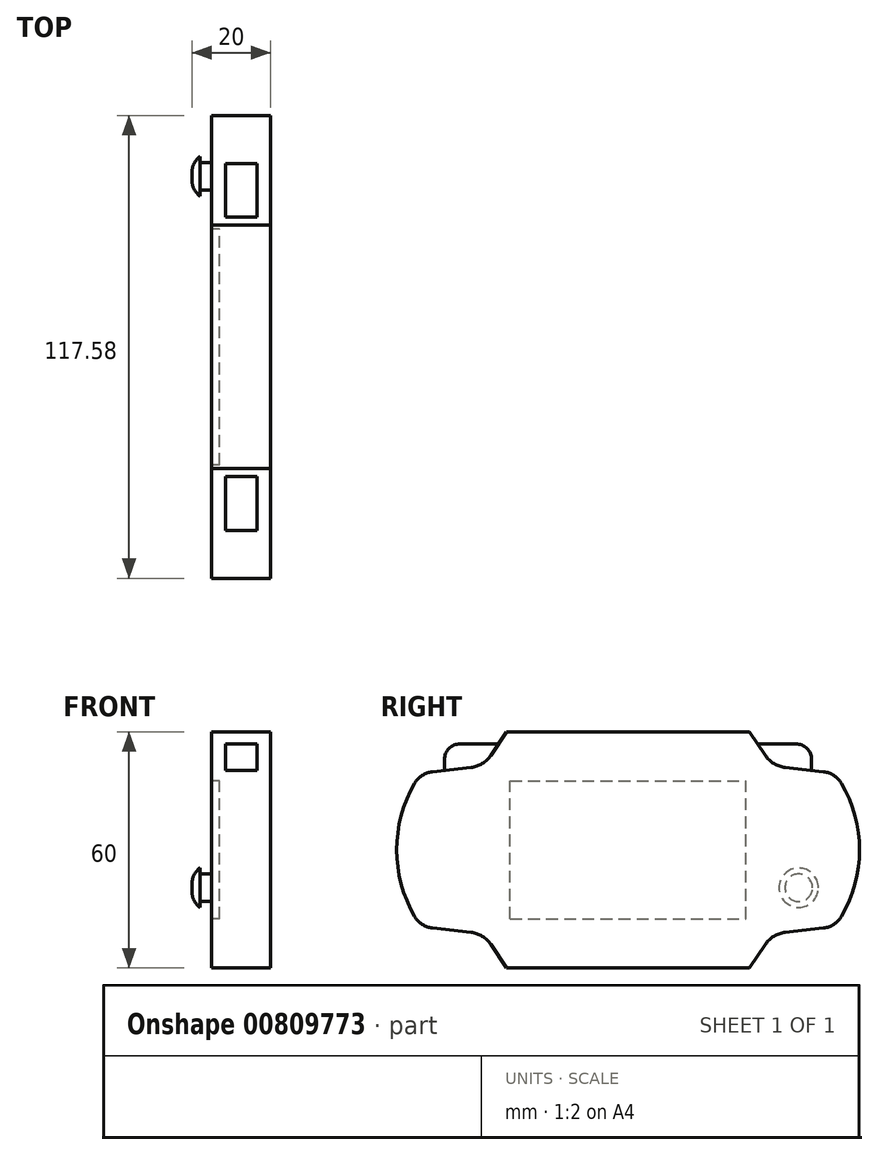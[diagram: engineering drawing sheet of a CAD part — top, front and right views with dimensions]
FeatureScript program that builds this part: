
annotation { "Feature Type Name" : "Feature", "Feature Type Description" : "" }
export const myFeature = defineFeature(function(context is Context, id is Id, definition is map)
    precondition{}
    {
        {
            var Q0;
            Q0=qCreatedBy(makeId("Right.planeOp"),FACE);
            var sketch = newSketch(context, id + "F0", { "sketchPlane" : qUnion([Q0])});
            skLineSegment(sketch, "E0.bottom", {"start": v(-30.9, -30) * mm, "end": v(30.9, -30) * mm});
            skLineSegment(sketch, "E0.top", {"start": v(-30.9, 30) * mm, "end": v(30.9, 30) * mm});
            skLineSegment(sketch, "E0.left", {"start": v(-52.5, -19.53) * mm, "end": v(-52.5, 19.53) * mm});
            skLineSegment(sketch, "E0.right", {"start": v(52.5, -19.53) * mm, "end": v(52.5, 19.53) * mm});
            skPoint(sketch, "E0.middle", {"position": v(0, 0) * mm});
            skLineSegment(sketch, "E1", {"start": v(49.7, 19.85) * mm, "end": v(46.21, 20.24) * mm});
            skLineSegment(sketch, "E2", {"start": v(34.87, 24.03) * mm, "end": v(30.9, 30) * mm});
            skPoint(sketch, "E3.visualSharp", {"position": v(36.68, 21.3) * mm});
            skArc(sketch, "E3.filletArc", {"start": v(34.87, 24.03) * mm, "mid": v(37.06, 21.92) * mm, "end": v(39.92, 20.94) * mm});
            skLineSegment(sketch, "E4", {"start": v(0, 39.51) * mm, "end": v(0, -39.4) * mm});
            skLineSegment(sketch, "E5.MirrorCS", {"start": v(-34.87, 24.03) * mm, "end": v(-30.9, 30) * mm});
            skPoint(sketch, "E6.MirrorP", {"position": v(-36.68, 21.3) * mm});
            skLineSegment(sketch, "E7.MirrorCS", {"start": v(-49.7, 19.85) * mm, "end": v(-46.21, 20.24) * mm});
            skArc(sketch, "E8.MirrorCS", {"start": v(-34.87, 24.03) * mm, "mid": v(-37.06, 21.92) * mm, "end": v(-39.92, 20.94) * mm});
            skLineSegment(sketch, "E9", {"start": v(46.21, 20.24) * mm, "end": v(39.92, 20.94) * mm});
            skLineSegment(sketch, "E10", {"start": v(59.6, 0) * mm, "end": v(-64.27, 0) * mm});
            skLineSegment(sketch, "E11.MirrorCS", {"start": v(49.7, -19.85) * mm, "end": v(46.21, -20.24) * mm});
            skLineSegment(sketch, "E12.MirrorCS", {"start": v(46.21, -20.24) * mm, "end": v(39.92, -20.94) * mm});
            skPoint(sketch, "E13.MirrorP", {"position": v(36.68, -21.3) * mm});
            skLineSegment(sketch, "E14.MirrorCS", {"start": v(34.87, -24.03) * mm, "end": v(30.9, -30) * mm});
            skArc(sketch, "E15.MirrorCS", {"start": v(34.87, -24.03) * mm, "mid": v(37.06, -21.92) * mm, "end": v(39.92, -20.94) * mm});
            skLineSegment(sketch, "E16.MirrorCS", {"start": v(-34.87, -24.03) * mm, "end": v(-30.9, -30) * mm});
            skArc(sketch, "E17.MirrorCS", {"start": v(-34.87, -24.03) * mm, "mid": v(-37.06, -21.92) * mm, "end": v(-39.92, -20.94) * mm});
            skLineSegment(sketch, "E18.MirrorCS", {"start": v(-49.7, -19.85) * mm, "end": v(-46.21, -20.24) * mm});
            skLineSegment(sketch, "E19", {"start": v(-46.21, 20.24) * mm, "end": v(-39.92, 20.94) * mm});
            skLineSegment(sketch, "E20", {"start": v(-46.21, -20.24) * mm, "end": v(-39.92, -20.94) * mm});
            skArc(sketch, "E21", {"start": v(54.2, -16.92) * mm, "mid": v(58.79, 0) * mm, "end": v(54.2, 16.92) * mm});
            skArc(sketch, "E22.MirrorCS", {"start": v(-54.2, -16.92) * mm, "mid": v(-58.79, 0) * mm, "end": v(-54.2, 16.92) * mm});
            skPoint(sketch, "E23.visualSharp", {"position": v(52.5, 19.53) * mm});
            skArc(sketch, "E23.filletArc", {"start": v(54.2, 16.92) * mm, "mid": v(52.3, 18.92) * mm, "end": v(49.7, 19.85) * mm});
            skPoint(sketch, "E24.visualSharp", {"position": v(52.5, -19.53) * mm});
            skArc(sketch, "E24.filletArc", {"start": v(49.7, -19.85) * mm, "mid": v(52.3, -18.92) * mm, "end": v(54.2, -16.92) * mm});
            skPoint(sketch, "E25.visualSharp", {"position": v(-52.5, 19.53) * mm});
            skArc(sketch, "E25.filletArc", {"start": v(-49.7, 19.85) * mm, "mid": v(-52.3, 18.92) * mm, "end": v(-54.2, 16.92) * mm});
            skPoint(sketch, "E26.visualSharp", {"position": v(-52.5, -19.53) * mm});
            skArc(sketch, "E26.filletArc", {"start": v(-54.2, -16.92) * mm, "mid": v(-52.3, -18.92) * mm, "end": v(-49.7, -19.85) * mm});
            skPoint(sketch, "E27.orphan", {"position": v(52.5, 30) * mm});
            skPoint(sketch, "E28.orphan", {"position": v(52.5, -30) * mm});
            skPoint(sketch, "E29.orphan", {"position": v(-52.5, -30) * mm});
            skPoint(sketch, "E30.orphan", {"position": v(-52.5, 30) * mm});
            skSolve(sketch);
        }
        {
            var Q0;
            Q0 = qSketchRegion(id + "F0", true);
            extrude(context, id + "F1", {"entities" : qUnion([Q0]), "endBound" : BoundingType.SYMMETRIC, "depth" : 15 * mm, "offsetDistance" : 25 * mm});
        }
        {
            var Q0;
            Q0=qCreatedBy(makeId("Right.planeOp"),FACE);
            var sketch = newSketch(context, id + "F2", { "sketchPlane" : qUnion([Q0])});
            skLineSegment(sketch, "E31.bottom", {"start": v(29.71, 18.85) * mm, "end": v(46.63, 18.85) * mm});
            skLineSegment(sketch, "E31.top", {"start": v(29.71, 26.92) * mm, "end": v(42.63, 26.92) * mm});
            skLineSegment(sketch, "E31.left", {"start": v(29.71, 18.85) * mm, "end": v(29.71, 26.92) * mm});
            skLineSegment(sketch, "E31.right", {"start": v(46.63, 18.85) * mm, "end": v(46.63, 22.92) * mm});
            skPoint(sketch, "E31.middle", {"position": v(38.17, 22.88) * mm});
            skLineSegment(sketch, "E32", {"start": v(0, 47.3) * mm, "end": v(0, -44.62) * mm});
            skLineSegment(sketch, "E33.MirrorCS", {"start": v(-29.71, 26.92) * mm, "end": v(-42.63, 26.92) * mm});
            skLineSegment(sketch, "E34.MirrorCS", {"start": v(-46.63, 18.85) * mm, "end": v(-46.63, 22.92) * mm});
            skLineSegment(sketch, "E35.MirrorCS", {"start": v(-29.71, 18.85) * mm, "end": v(-29.71, 26.92) * mm});
            skLineSegment(sketch, "E36.MirrorCS", {"start": v(-29.71, 18.85) * mm, "end": v(-46.63, 18.85) * mm});
            skPoint(sketch, "E37.visualSharp", {"position": v(46.63, 26.92) * mm});
            skArc(sketch, "E37.filletArc", {"start": v(46.63, 22.92) * mm, "mid": v(45.46, 25.75) * mm, "end": v(42.63, 26.92) * mm});
            skPoint(sketch, "E38.visualSharp", {"position": v(-46.63, 26.92) * mm});
            skArc(sketch, "E38.filletArc", {"start": v(-42.63, 26.92) * mm, "mid": v(-45.46, 25.75) * mm, "end": v(-46.63, 22.92) * mm});
            skSolve(sketch);
        }
        {
            var Q0;
            Q0=makeQuery(id+"F2.imprint","IMPRINT",FACE,{"disambiguationData":[TD([[makeQuery(id+"F2.imprint","IMPRINT",EDGE,{"derivedFrom":sQuery(id+"F2.wireOp",EDGE,"E31.bottom")}),1.0]])]});
            var Q1;
            Q1=makeQuery(id+"F2.imprint","IMPRINT",FACE,{"disambiguationData":[TD([[makeQuery(id+"F2.imprint","IMPRINT",EDGE,{"derivedFrom":sQuery(id+"F2.wireOp",EDGE,"E33.MirrorCS")}),1.0]])]});
            var Q2;
            Q2 = qConstructionFilter(qBodyType(qCreatedBy(id + "F2" ,EDGE), BodyType.WIRE), ConstructionObject.NO);
            extrude(context, id + "F3", {"entities" : qUnion([Q0, Q1]), "operationType" : NewBodyOperationType.ADD, "surfaceEntities" : qUnion([Q2]), "endBound" : BoundingType.SYMMETRIC, "depth" : 8 * mm, "offsetDistance" : 25 * mm});
        }
        {
            var Q0;
            Q0=makeQuery(id+"F1.opExtrude","CAP_FACE",FACE,{"disambiguationData":[OSD([sQuery(id+"F0.wireOp",EDGE,"E0.bottom"),sQuery(id+"F0.wireOp",EDGE,"E0.top"),sQuery(id+"F0.wireOp",EDGE,"E1"),sQuery(id+"F0.wireOp",EDGE,"E2"),sQuery(id+"F0.wireOp",EDGE,"E3.filletArc"),sQuery(id+"F0.wireOp",EDGE,"E5.MirrorCS"),sQuery(id+"F0.wireOp",EDGE,"E7.MirrorCS"),sQuery(id+"F0.wireOp",EDGE,"E8.MirrorCS"),sQuery(id+"F0.wireOp",EDGE,"E9"),sQuery(id+"F0.wireOp",EDGE,"E11.MirrorCS"),sQuery(id+"F0.wireOp",EDGE,"E12.MirrorCS"),sQuery(id+"F0.wireOp",EDGE,"E14.MirrorCS"),sQuery(id+"F0.wireOp",EDGE,"E15.MirrorCS"),sQuery(id+"F0.wireOp",EDGE,"E16.MirrorCS"),sQuery(id+"F0.wireOp",EDGE,"E17.MirrorCS"),sQuery(id+"F0.wireOp",EDGE,"E18.MirrorCS"),sQuery(id+"F0.wireOp",EDGE,"E19"),sQuery(id+"F0.wireOp",EDGE,"E20"),sQuery(id+"F0.wireOp",EDGE,"E21"),sQuery(id+"F0.wireOp",EDGE,"E22.MirrorCS"),sQuery(id+"F0.wireOp",EDGE,"E23.filletArc"),sQuery(id+"F0.wireOp",EDGE,"E24.filletArc"),sQuery(id+"F0.wireOp",EDGE,"E25.filletArc"),sQuery(id+"F0.wireOp",EDGE,"E26.filletArc")])],"isStart":true});
            var sketch = newSketch(context, id + "F4", { "sketchPlane" : qUnion([Q0])});
            skLineSegment(sketch, "E39.bottom", {"start": v(30, -17.5) * mm, "end": v(-30, -17.5) * mm});
            skLineSegment(sketch, "E39.top", {"start": v(30, 17.5) * mm, "end": v(-30, 17.5) * mm});
            skLineSegment(sketch, "E39.left", {"start": v(30, -17.5) * mm, "end": v(30, 17.5) * mm});
            skLineSegment(sketch, "E39.right", {"start": v(-30, -17.5) * mm, "end": v(-30, 17.5) * mm});
            skPoint(sketch, "E39.middle", {"position": v(0, 0) * mm});
            skSolve(sketch);
        }
        {
            var Q0;
            Q0=makeQuery(id+"F4.imprint","IMPRINT",FACE,{"disambiguationData":[TD([[makeQuery(id+"F4.imprint","IMPRINT",EDGE,{"derivedFrom":sQuery(id+"F4.wireOp",EDGE,"E39.bottom")}),1.0]])]});
            var sketch = newSketch(context, id + "F5", { "sketchPlane" : qUnion([Q0])});
            skCircle(sketch, "E40", {"center": v(-43.37, -9.62) * mm, "radius": 3.5 * mm});
            skSolve(sketch);
        }
        {
            var Q0;
            Q0 = qSketchRegion(id + "F5", true);
            extrude(context, id + "F6", {"entities" : qUnion([Q0]), "operationType" : NewBodyOperationType.ADD, "depth" : 3 * mm, "offsetDistance" : 25 * mm});
        }
        {
            var Q0;
            Q0=makeQuery(id+"F6.opExtrude","CAP_FACE",FACE,{"disambiguationData":[OSD([sQuery(id+"F5.wireOp",EDGE,"E40")])],"isStart":false});
            var sketch = newSketch(context, id + "F7", { "sketchPlane" : qUnion([Q0])});
            skCircle(sketch, "E41", {"center": v(-43.37, -9.62) * mm, "radius": 5 * mm});
            skSolve(sketch);
        }
        {
            var Q0;
            Q0 = qSketchRegion(id + "F7", true);
            extrude(context, id + "F8", {"entities" : qUnion([Q0]), "operationType" : NewBodyOperationType.ADD, "depth" : 2 * mm, "offsetDistance" : 25 * mm});
        }
        {
            var Q0;
            Q0=makeQuery(id+"F8.opExtrude","CAP_FACE",FACE,{"disambiguationData":[OSD([sQuery(id+"F7.wireOp",EDGE,"E41")])],"isStart":false});
            fillet(context, id + "F9", {"entities" : qUnion([Q0]), "radius" : 5 * mm, "tangentPropagation" : true, "allowEdgeOverflow" : false});
        }
        {
            var Q0;
            Q0=makeQuery(id+"F4.imprint","IMPRINT",FACE,{"disambiguationData":[TD([[makeQuery(id+"F4.imprint","IMPRINT",EDGE,{"derivedFrom":sQuery(id+"F4.wireOp",EDGE,"E39.bottom")}),-1.0]])]});
            extrude(context, id + "F10", {"entities" : qUnion([Q0]), "operationType" : NewBodyOperationType.REMOVE, "oppositeDirection" : true, "depth" : 2 * mm, "offsetDistance" : 25 * mm});
        }
    });
